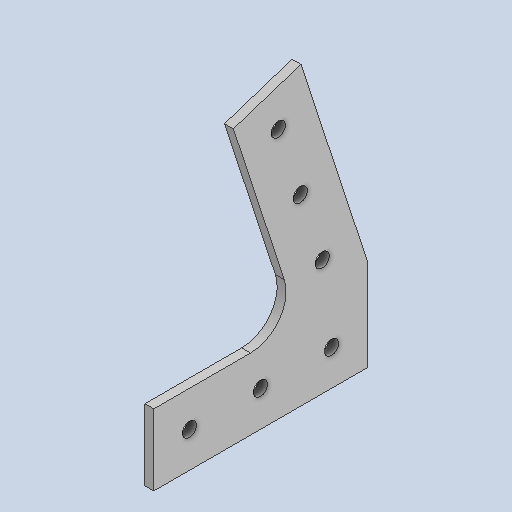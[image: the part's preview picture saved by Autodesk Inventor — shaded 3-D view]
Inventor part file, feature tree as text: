
AUTODESK INVENTOR PART (.ipt)
format: ipt  version: 2024 (Build 280153000, 153)  size: 159,744 bytes
history: native  units: in
note: dims shown in document units (in); Inventor stores cm internally (conversion verified against a paired STEP export)
features: extrude x1, fillet x1
ambient origin geometry x8: Origin, YZ Plane, XZ Plane, XY Plane, X Axis, Y Axis, Z Axis, Center Point
bodies: Solid1 (feature_tree)
feature tree (2):
  extrude  "Extrusion1"  Depth=1.0in
  fillet  "Fillet1"  Radius=3.0in
